# Revit family: VL2S-MRM100-7DASW840B0300
name_source: partatom
category: Leuchten
units: mm (PartAtom-declared; Revit-internal decimal feet)

## family parameters
Basisbauteil = Fläche
Beim Laden mit Abzugskörper schneiden = Nein
Bemaßung runder Anschluss = Durchmesser verwenden
Gemeinsam genutzt = Nein
Lichtquelle = Ja
OmniClass-Nummer = 23.80.70.11
OmniClass-Titel = Luminaries for Internal Lighting
Raumberechnungspunkt = Nein
Teiletyp = Normal

## types (1)
- VL2S-MRM100-7DASW840B0300
    Baugruppenkennzeichen = D5020200
    Datei für fotometrisches Netz = VLG-MRM.IES
    Emissionsform beim Rendern sichtbar = Nein
    Farbfilter = 16777215
    Farbtemperaturverschiebung bei Dämpfen der Lampe = <Keine Auswahl>
    Hersteller = RIDI Leuchten GmbH
    Lampe = LED
    Modell = 2560008SW
    Neigungswinkel = 90.00°
    Scheinlast = 22 VA
    URL = www.ridi.de
    Von Breite des Rechtecks ausssenden = 528 mm  [stored 1.73228 ft]
    Von Länge des Rechtecks aussenden = 48 mm  [stored 0.15748 ft]
    Vorgabe-Ansicht = 0 mm  [stored 0 ft]
    brand = RIDI
    conformity mark = CE
    electrical safety class = 1
    height = 67 mm
    ingress protection (IP) code = IP40
    length = 1000 mm  [stored 3.28084 ft]
    nominal frequency = 50-60Hz
    nominal voltage = 230
    product name = VL2S-MRM100-7DASW840B0300
    rated input power = 22
    voltage type (AC, DC, UC) = AC
    weight = 1,3kg
    width = 67 mm

note: [stored X ft] marks values corroborated as IEEE doubles in the binary element streams (Revit-internal decimal feet)
